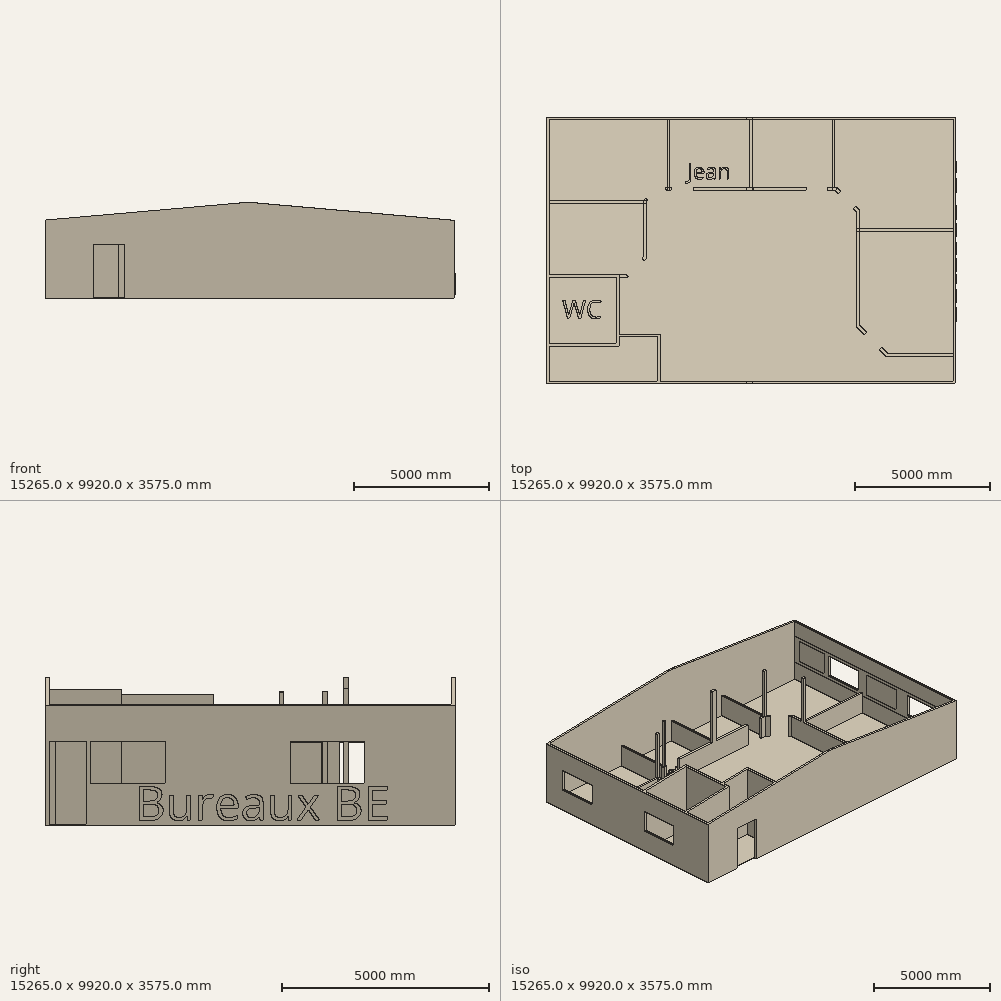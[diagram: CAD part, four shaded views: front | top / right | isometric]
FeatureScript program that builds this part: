
annotation { "Feature Type Name" : "Feature", "Feature Type Description" : "" }
export const myFeature = defineFeature(function(context is Context, id is Id, definition is map)
    precondition{}
    {
        {
            var Q0;
            Q0=qCreatedBy(makeId("Top.planeOp"),FACE);
            var sketch = newSketch(context, id + "F0", { "sketchPlane" : qUnion([Q0])});
            skLineSegment(sketch, "E0.bottom", {"start": v(0, 0) * mm, "end": v(-15040, 0) * mm});
            skLineSegment(sketch, "E0.top", {"start": v(0, 9720) * mm, "end": v(-15040, 9720) * mm});
            skLineSegment(sketch, "E0.left", {"start": v(0, 0) * mm, "end": v(0, 9720) * mm});
            skLineSegment(sketch, "E0.right", {"start": v(-15040, 0) * mm, "end": v(-15040, 9720) * mm});
            skSolve(sketch);
        }
        {
            var Q0;
            Q0 = qSketchRegion(id + "F0", true);
            extrude(context, id + "F1", {"entities" : qUnion([Q0]), "depth" : 25 * mm});
        }
        {
            var Q0;
            Q0=makeQuery(id+"F1.opExtrude","CAP_FACE",FACE,{"disambiguationData":[OSD([sQuery(id+"F0.wireOp",EDGE,"E0.bottom"),sQuery(id+"F0.wireOp",EDGE,"E0.top"),sQuery(id+"F0.wireOp",EDGE,"E0.left"),sQuery(id+"F0.wireOp",EDGE,"E0.right")])],"isStart":false});
            var sketch = newSketch(context, id + "F2", { "sketchPlane" : qUnion([Q0])});
            skLineSegment(sketch, "E1", {"start": v(-15040, 1300) * mm, "end": v(-12440, 1300) * mm});
            skLineSegment(sketch, "E2", {"start": v(-12440, 1300) * mm, "end": v(-12440, 1650) * mm});
            skLineSegment(sketch, "E3", {"start": v(-12440, 1650) * mm, "end": v(-10990, 1650) * mm});
            skLineSegment(sketch, "E4", {"start": v(-10990, 1650) * mm, "end": v(-10990, 0) * mm});
            skLineSegment(sketch, "E5", {"start": v(-10990, 0) * mm, "end": v(-10890, 0) * mm});
            skLineSegment(sketch, "E6", {"start": v(-10890, 0) * mm, "end": v(-10890, 1750) * mm});
            skLineSegment(sketch, "E7", {"start": v(-10890, 1750) * mm, "end": v(-12540, 1750) * mm});
            skLineSegment(sketch, "E8", {"start": v(-12540, 1750) * mm, "end": v(-12540, 1400) * mm});
            skLineSegment(sketch, "E9", {"start": v(-12540, 1400) * mm, "end": v(-15040, 1400) * mm});
            skLineSegment(sketch, "E10", {"start": v(-15040, 1400) * mm, "end": v(-15040, 1300) * mm});
            skLineSegment(sketch, "E11.bottom", {"start": v(-15040, 0) * mm, "end": v(0, 0) * mm});
            skLineSegment(sketch, "E11.top", {"start": v(-15040, 9720) * mm, "end": v(0, 9720) * mm});
            skLineSegment(sketch, "E11.left", {"start": v(-15040, 0) * mm, "end": v(-15040, 9720) * mm});
            skLineSegment(sketch, "E11.right", {"start": v(0, 0) * mm, "end": v(0, 9720) * mm});
            skLineSegment(sketch, "E12.bottom", {"start": v(100, 9820) * mm, "end": v(-15140, 9820) * mm});
            skLineSegment(sketch, "E12.top", {"start": v(100, -100) * mm, "end": v(-15140, -100) * mm});
            skLineSegment(sketch, "E12.left", {"start": v(100, 9820) * mm, "end": v(100, -100) * mm});
            skLineSegment(sketch, "E12.right", {"start": v(-15140, 9820) * mm, "end": v(-15140, -100) * mm});
            skLineSegment(sketch, "E13", {"start": v(0, 900) * mm, "end": v(-2479.9, 900) * mm});
            skLineSegment(sketch, "E14", {"start": v(-2479.9, 900) * mm, "end": v(-3615, 2035.1) * mm});
            skLineSegment(sketch, "E15", {"start": v(-3615, 2035.1) * mm, "end": v(-3615, 4846.83) * mm});
            skLineSegment(sketch, "E16.0", {"start": v(-3500, 2082.73) * mm, "end": v(-3500, 5555) * mm});
            skLineSegment(sketch, "E16.1", {"start": v(-2432.27, 1015) * mm, "end": v(-3500, 2082.73) * mm});
            skLineSegment(sketch, "E16.2", {"start": v(0, 1015) * mm, "end": v(-2432.27, 1015) * mm});
            skLineSegment(sketch, "E17", {"start": v(-3500, 5555) * mm, "end": v(0, 5555) * mm});
            skLineSegment(sketch, "E18", {"start": v(0, 5555) * mm, "end": v(0, 5670) * mm});
            skLineSegment(sketch, "E19", {"start": v(0, 5670) * mm, "end": v(-3500, 5670) * mm});
            skLineSegment(sketch, "E20", {"start": v(-3500, 5670) * mm, "end": v(-3500, 6371.47) * mm});
            skLineSegment(sketch, "E21", {"start": v(-3615, 4846.83) * mm, "end": v(-3615, 6323.84) * mm});
            skLineSegment(sketch, "E22", {"start": v(-3615, 6323.84) * mm, "end": v(-4396.16, 7105) * mm});
            skLineSegment(sketch, "E23", {"start": v(-4400, 7220) * mm, "end": v(-4400, 9720) * mm});
            skLineSegment(sketch, "E24", {"start": v(-4400, 9720) * mm, "end": v(-4475, 9720) * mm});
            skLineSegment(sketch, "E25", {"start": v(-4475, 9720) * mm, "end": v(-4475, 7220) * mm});
            skLineSegment(sketch, "E26", {"start": v(-4475, 7220) * mm, "end": v(-7475, 7220) * mm});
            skLineSegment(sketch, "E27", {"start": v(-4396.16, 7105) * mm, "end": v(-10610.2, 7105) * mm});
            skLineSegment(sketch, "E28", {"start": v(-4400, 7220) * mm, "end": v(-4348.53, 7220) * mm});
            skLineSegment(sketch, "E29", {"start": v(-4348.53, 7220) * mm, "end": v(-3500, 6371.47) * mm});
            skLineSegment(sketch, "E30", {"start": v(-7475, 7220) * mm, "end": v(-7475, 9720) * mm});
            skLineSegment(sketch, "E31", {"start": v(-7475, 9720) * mm, "end": v(-7565, 9720) * mm});
            skLineSegment(sketch, "E32", {"start": v(-7565, 9720) * mm, "end": v(-7565, 7220) * mm});
            skLineSegment(sketch, "E33", {"start": v(-7565, 7220) * mm, "end": v(-10565, 7220) * mm});
            skLineSegment(sketch, "E34", {"start": v(-10565, 7220) * mm, "end": v(-10565, 9720) * mm});
            skLineSegment(sketch, "E35", {"start": v(-10565, 9720) * mm, "end": v(-10640, 9720) * mm});
            skLineSegment(sketch, "E36", {"start": v(-10640, 9720) * mm, "end": v(-10640, 7220) * mm});
            skLineSegment(sketch, "E37", {"start": v(-10640, 7220) * mm, "end": v(-11540, 6720) * mm});
            skLineSegment(sketch, "E38", {"start": v(-11540, 6720) * mm, "end": v(-11540, 6720) * mm});
            skLineSegment(sketch, "E39", {"start": v(-11540, 6720) * mm, "end": v(-15040, 6720) * mm});
            skLineSegment(sketch, "E40", {"start": v(-15040, 6720) * mm, "end": v(-15040, 6605) * mm});
            skLineSegment(sketch, "E41", {"start": v(-15040, 6605) * mm, "end": v(-11540, 6605) * mm});
            skLineSegment(sketch, "E42", {"start": v(-11540, 6605) * mm, "end": v(-11540, 4595.6) * mm});
            skLineSegment(sketch, "E43", {"start": v(-11540, 4595.6) * mm, "end": v(-12165.6, 3970) * mm});
            skLineSegment(sketch, "E44", {"start": v(-12165.6, 3970) * mm, "end": v(-15040, 3970) * mm});
            skLineSegment(sketch, "E45", {"start": v(-15040, 3970) * mm, "end": v(-15040, 3855) * mm});
            skLineSegment(sketch, "E46", {"start": v(-15040, 3855) * mm, "end": v(-12117.96, 3855) * mm});
            skLineSegment(sketch, "E47", {"start": v(-12117.96, 3855) * mm, "end": v(-11425, 4547.96) * mm});
            skLineSegment(sketch, "E48", {"start": v(-11425, 4547.96) * mm, "end": v(-11425, 6652.33) * mm});
            skLineSegment(sketch, "E49", {"start": v(-11425, 6652.33) * mm, "end": v(-10610.2, 7105) * mm});
            skLineSegment(sketch, "E50", {"start": v(-12540, 1750) * mm, "end": v(-12540, 3855) * mm});
            skLineSegment(sketch, "E51", {"start": v(-12440, 1750) * mm, "end": v(-12440, 3855) * mm});
            skLineSegment(sketch, "E52", {"start": v(-12440, 3855) * mm, "end": v(-12540, 3855) * mm});
            skLineSegment(sketch, "E53", {"start": v(-12440, 1750) * mm, "end": v(-12540, 1750) * mm});
            skSolve(sketch);
        }
        {
            var Q0;
            Q0 = qSketchRegion(id + "F2", true);
            var Q1;
            {var subQ3=sQuery(id+"F2.wireOp",EDGE,"E1");Q1=makeQuery(id+"F2.imprint","IMPRINT",FACE,{"disambiguationData":[TD([[makeQuery(id+"F2.imprint","IMPRINT",EDGE,{"derivedFrom":subQ3}),1.0]])]});}
            var Q2;
            Q2=makeQuery(id+"F2.imprint","IMPRINT",FACE,{"disambiguationData":[TD([[makeQuery(id+"F2.imprint","IMPRINT",EDGE,{"derivedFrom":sQuery(id+"F2.wireOp",EDGE,"E50")}),-1.0]])]});
            var Q3;
            {var subQ2=sQuery(id+"F2.wireOp",EDGE,"E13");Q3=makeQuery(id+"F2.imprint","IMPRINT",FACE,{"disambiguationData":[TD([[makeQuery(id+"F2.imprint","IMPRINT",EDGE,{"derivedFrom":subQ2}),-1.0]])]});}
            extrude(context, id + "F3", {"entities" : qUnion([Q0, Q1, Q2, Q3]), "operationType" : NewBodyOperationType.ADD, "depth" : 3550 * mm, "hasSecondDirection" : true, "secondDirectionOppositeDirection" : true, "secondDirectionDepth" : 25 * mm});
        }
        {
            var Q0;
            Q0=makeQuery(id+"F3.opExtrude","SWEPT_FACE",FACE,{"disambiguationData":[OSD([sQuery(id+"F2.wireOp",EDGE,"E12.left")])]});
            var sketch = newSketch(context, id + "F4", { "sketchPlane" : qUnion([Q0])});
            skLineSegment(sketch, "E54.bottom", {"start": v(1000, 2025) * mm, "end": v(2800, 2025) * mm});
            skLineSegment(sketch, "E54.top", {"start": v(1000, 1025) * mm, "end": v(2800, 1025) * mm});
            skLineSegment(sketch, "E54.left", {"start": v(1000, 2025) * mm, "end": v(1000, 1025) * mm});
            skLineSegment(sketch, "E54.right", {"start": v(2800, 2025) * mm, "end": v(2800, 1025) * mm});
            skLineSegment(sketch, "E55.bottom", {"start": v(5830, 2025) * mm, "end": v(7630, 2025) * mm});
            skLineSegment(sketch, "E55.top", {"start": v(5830, 1025) * mm, "end": v(7630, 1025) * mm});
            skLineSegment(sketch, "E55.left", {"start": v(5830, 2025) * mm, "end": v(5830, 1025) * mm});
            skLineSegment(sketch, "E55.right", {"start": v(7630, 2025) * mm, "end": v(7630, 1025) * mm});
            skSolve(sketch);
        }
        {
            var Q0;
            Q0 = qSketchRegion(id + "F4", true);
            var Q1;
            {var subQ0=sQuery(id+"F2.wireOp",EDGE,"E11.right");Q1=makeQuery(id+"F3.opExtrude","SWEPT_FACE",FACE,{"disambiguationData":[OSD([subQ0]),TDD([makeQuery(id+"F2.imprint","IMPRINT",EDGE,{"disambiguationData":[TD([[makeQuery(id+"F2.imprint","INTERSECT",VERTEX,{"derivedFrom":[subQ0,sQuery(id+"F2.wireOp",EDGE,"E16.2")]}),-1.0]])],"derivedFrom":subQ0})])]});}
            extrude(context, id + "F5", {"entities" : qUnion([Q0]), "operationType" : NewBodyOperationType.REMOVE, "endBound" : BoundingType.UP_TO_SURFACE, "oppositeDirection" : true, "endBoundEntityFace" : qUnion([Q1]), "depth" : 25 * mm});
        }
        {
            var Q0;
            Q0=makeQuery(id+"F3.opExtrude","SWEPT_FACE",FACE,{"disambiguationData":[OSD([sQuery(id+"F2.wireOp",EDGE,"E12.right")])]});
            var sketch = newSketch(context, id + "F6", { "sketchPlane" : qUnion([Q0])});
            skLineSegment(sketch, "E56.bottom", {"start": v(-8820, 2000) * mm, "end": v(-7020, 2000) * mm});
            skLineSegment(sketch, "E56.top", {"start": v(-8820, 1000) * mm, "end": v(-7020, 1000) * mm});
            skLineSegment(sketch, "E56.left", {"start": v(-8820, 2000) * mm, "end": v(-8820, 1000) * mm});
            skLineSegment(sketch, "E56.right", {"start": v(-7020, 2000) * mm, "end": v(-7020, 1000) * mm});
            skLineSegment(sketch, "E57.bottom", {"start": v(-3810, 2000) * mm, "end": v(-2010, 2000) * mm});
            skLineSegment(sketch, "E57.top", {"start": v(-3810, 1000) * mm, "end": v(-2010, 1000) * mm});
            skLineSegment(sketch, "E57.left", {"start": v(-3810, 2000) * mm, "end": v(-3810, 1000) * mm});
            skLineSegment(sketch, "E57.right", {"start": v(-2010, 2000) * mm, "end": v(-2010, 1000) * mm});
            skSolve(sketch);
        }
        {
            var Q0;
            Q0 = qSketchRegion(id + "F6", true);
            var Q1;
            {var subQ0=sQuery(id+"F2.wireOp",EDGE,"E11.left");Q1=makeQuery(id+"F3.opExtrude","SWEPT_FACE",FACE,{"disambiguationData":[OSD([subQ0]),TDD([makeQuery(id+"F2.imprint","IMPRINT",EDGE,{"disambiguationData":[TD([[makeQuery(id+"F2.imprint","INTERSECT",VERTEX,{"derivedFrom":[subQ0,sQuery(id+"F2.wireOp",EDGE,"E40"),sQuery(id+"F2.wireOp",EDGE,"E41")]}),1.0]])],"derivedFrom":subQ0})])]});}
            extrude(context, id + "F7", {"entities" : qUnion([Q0]), "operationType" : NewBodyOperationType.REMOVE, "endBound" : BoundingType.UP_TO_SURFACE, "oppositeDirection" : true, "endBoundEntityFace" : qUnion([Q1]), "depth" : 25 * mm});
        }
        {
            var Q0;
            Q0=makeQuery(id+"F3.opExtrude","SWEPT_FACE",FACE,{"disambiguationData":[OSD([sQuery(id+"F2.wireOp",EDGE,"E12.top")])]});
            var sketch = newSketch(context, id + "F8", { "sketchPlane" : qUnion([Q0])});
            skLineSegment(sketch, "E58.bottom", {"start": v(-13340, 0) * mm, "end": v(-12190, 0) * mm});
            skLineSegment(sketch, "E58.top", {"start": v(-13340, 2000) * mm, "end": v(-12190, 2000) * mm});
            skLineSegment(sketch, "E58.left", {"start": v(-13340, 0) * mm, "end": v(-13340, 2000) * mm});
            skLineSegment(sketch, "E58.right", {"start": v(-12190, 0) * mm, "end": v(-12190, 2000) * mm});
            skSolve(sketch);
        }
        {
            var Q0;
            Q0 = qSketchRegion(id + "F8", true);
            var Q1;
            {var subQ0=sQuery(id+"F2.wireOp",EDGE,"E11.bottom");Q1=makeQuery(id+"F3.opExtrude","SWEPT_FACE",FACE,{"disambiguationData":[OSD([subQ0]),TDD([makeQuery(id+"F2.imprint","IMPRINT",EDGE,{"disambiguationData":[TD([[makeQuery(id+"F2.imprint","INTERSECT",VERTEX,{"derivedFrom":[subQ0,sQuery(id+"F2.wireOp",EDGE,"E11.left")]}),1.0]])],"derivedFrom":subQ0})])]});}
            extrude(context, id + "F9", {"entities" : qUnion([Q0]), "operationType" : NewBodyOperationType.REMOVE, "endBound" : BoundingType.UP_TO_SURFACE, "oppositeDirection" : true, "endBoundEntityFace" : qUnion([Q1]), "depth" : 25 * mm});
        }
        {
            var Q0;
            Q0=makeQuery(id+"F3.opExtrude","SWEPT_FACE",FACE,{"disambiguationData":[OSD([sQuery(id+"F2.wireOp",EDGE,"E6")])]});
            var sketch = newSketch(context, id + "F10", { "sketchPlane" : qUnion([Q0])});
            skLineSegment(sketch, "E59.bottom", {"start": v(930, 25) * mm, "end": v(130, 25) * mm});
            skLineSegment(sketch, "E59.top", {"start": v(930, 2025) * mm, "end": v(130, 2025) * mm});
            skLineSegment(sketch, "E59.left", {"start": v(930, 25) * mm, "end": v(930, 2025) * mm});
            skLineSegment(sketch, "E59.right", {"start": v(130, 25) * mm, "end": v(130, 2025) * mm});
            skSolve(sketch);
        }
        {
            var Q0;
            Q0 = qSketchRegion(id + "F10", true);
            extrude(context, id + "F11", {"entities" : qUnion([Q0]), "operationType" : NewBodyOperationType.REMOVE, "endBound" : BoundingType.UP_TO_NEXT, "oppositeDirection" : true, "depth" : 25 * mm});
        }
        {
            var Q0;
            Q0=makeQuery(id+"F3.opExtrude","SWEPT_FACE",FACE,{"disambiguationData":[OSD([sQuery(id+"F2.wireOp",EDGE,"E12.bottom")])]});
            var sketch = newSketch(context, id + "F12", { "sketchPlane" : qUnion([Q0])});
            skLineSegment(sketch, "E60", {"start": v(7680, 3575) * mm, "end": v(15140, 2919.97) * mm});
            skLineSegment(sketch, "E61", {"start": v(15140, 2919.97) * mm, "end": v(15140, 3575) * mm});
            skLineSegment(sketch, "E62", {"start": v(15140, 3575) * mm, "end": v(7680, 3575) * mm});
            skLineSegment(sketch, "E63", {"start": v(7480, 3575) * mm, "end": v(-100, 3575) * mm});
            skLineSegment(sketch, "E64", {"start": v(-100, 3575) * mm, "end": v(-100, 2909.44) * mm});
            skLineSegment(sketch, "E65", {"start": v(-100, 2909.44) * mm, "end": v(7480, 3575) * mm});
            skSolve(sketch);
        }
        {
            var Q0;
            Q0 = qSketchRegion(id + "F12", true);
            extrude(context, id + "F13", {"entities" : qUnion([Q0]), "operationType" : NewBodyOperationType.REMOVE, "endBound" : BoundingType.THROUGH_ALL, "oppositeDirection" : true, "depth" : 25 * mm});
        }
        {
            var Q0;
            {var subQ0=sQuery(id+"F2.wireOp",EDGE,"E11.right");Q0=makeQuery(id+"F3.opExtrude","SWEPT_FACE",FACE,{"disambiguationData":[OSD([subQ0]),TDD([makeQuery(id+"F2.imprint","IMPRINT",EDGE,{"disambiguationData":[TD([[makeQuery(id+"F2.imprint","INTERSECT",VERTEX,{"derivedFrom":[sQuery(id+"F2.wireOp",EDGE,"E11.bottom"),subQ0]}),-1.0]])],"derivedFrom":subQ0})])]});}
            var sketch = newSketch(context, id + "F14", { "sketchPlane" : qUnion([Q0])});
            skLineSegment(sketch, "E66.bottom", {"start": v(0, 25) * mm, "end": v(-900, 25) * mm});
            skLineSegment(sketch, "E66.top", {"start": v(0, 2025) * mm, "end": v(-900, 2025) * mm});
            skLineSegment(sketch, "E66.left", {"start": v(0, 25) * mm, "end": v(0, 2025) * mm});
            skLineSegment(sketch, "E66.right", {"start": v(-900, 25) * mm, "end": v(-900, 2025) * mm});
            skSolve(sketch);
        }
        {
            var Q0;
            Q0 = qSketchRegion(id + "F14", true);
            extrude(context, id + "F15", {"entities" : qUnion([Q0]), "operationType" : NewBodyOperationType.REMOVE, "endBound" : BoundingType.UP_TO_NEXT, "oppositeDirection" : true, "depth" : 25 * mm});
        }
        {
            var Q0;
            {var subQ0=sQuery(id+"F2.wireOp",EDGE,"E32");var subQ1=sQuery(id+"F2.wireOp",EDGE,"E27");var subQ2=sQuery(id+"F2.wireOp",EDGE,"E12.bottom");var subQ3=sQuery(id+"F2.wireOp",EDGE,"E11.top");var subQ4=sQuery(id+"F2.wireOp",EDGE,"E34");var subQ5=sQuery(id+"F2.wireOp",EDGE,"E33");Q0=makeQuery(id+"F13.boolean.opBoolean","SPLIT",FACE,{"disambiguationData":[TD([makeQuery(id+"F3.opExtrude","SWEPT_FACE",FACE,{"disambiguationData":[OSD([subQ2])]})])],"derivedFrom":makeQuery(id+"F3.opExtrude","CAP_FACE",FACE,{"disambiguationData":[OSD([sQuery(id+"F2.wireOp",EDGE,"E1"),sQuery(id+"F2.wireOp",EDGE,"E2"),sQuery(id+"F2.wireOp",EDGE,"E3"),sQuery(id+"F2.wireOp",EDGE,"E4"),sQuery(id+"F2.wireOp",EDGE,"E6"),sQuery(id+"F2.wireOp",EDGE,"E7"),sQuery(id+"F2.wireOp",EDGE,"E8"),sQuery(id+"F2.wireOp",EDGE,"E9"),sQuery(id+"F2.wireOp",EDGE,"E11.bottom"),subQ3,sQuery(id+"F2.wireOp",EDGE,"E11.left"),sQuery(id+"F2.wireOp",EDGE,"E11.right"),subQ2,sQuery(id+"F2.wireOp",EDGE,"E12.top"),sQuery(id+"F2.wireOp",EDGE,"E12.left"),sQuery(id+"F2.wireOp",EDGE,"E12.right"),sQuery(id+"F2.wireOp",EDGE,"E13"),sQuery(id+"F2.wireOp",EDGE,"E14"),sQuery(id+"F2.wireOp",EDGE,"E15"),sQuery(id+"F2.wireOp",EDGE,"E16.0"),sQuery(id+"F2.wireOp",EDGE,"E16.1"),sQuery(id+"F2.wireOp",EDGE,"E16.2"),sQuery(id+"F2.wireOp",EDGE,"E17"),sQuery(id+"F2.wireOp",EDGE,"E19"),sQuery(id+"F2.wireOp",EDGE,"E20"),sQuery(id+"F2.wireOp",EDGE,"E21"),sQuery(id+"F2.wireOp",EDGE,"E22"),sQuery(id+"F2.wireOp",EDGE,"E23"),sQuery(id+"F2.wireOp",EDGE,"E25"),sQuery(id+"F2.wireOp",EDGE,"E26"),subQ1,sQuery(id+"F2.wireOp",EDGE,"E28"),sQuery(id+"F2.wireOp",EDGE,"E29"),sQuery(id+"F2.wireOp",EDGE,"E30"),subQ0,subQ5,subQ4,sQuery(id+"F2.wireOp",EDGE,"E36"),sQuery(id+"F2.wireOp",EDGE,"E37"),sQuery(id+"F2.wireOp",EDGE,"E38"),sQuery(id+"F2.wireOp",EDGE,"E39"),sQuery(id+"F2.wireOp",EDGE,"E41"),sQuery(id+"F2.wireOp",EDGE,"E42"),sQuery(id+"F2.wireOp",EDGE,"E43"),sQuery(id+"F2.wireOp",EDGE,"E44"),sQuery(id+"F2.wireOp",EDGE,"E46"),sQuery(id+"F2.wireOp",EDGE,"E47"),sQuery(id+"F2.wireOp",EDGE,"E48"),sQuery(id+"F2.wireOp",EDGE,"E49"),sQuery(id+"F2.wireOp",EDGE,"E50"),sQuery(id+"F2.wireOp",EDGE,"E51")])],"isStart":false})});}
            var sketch = newSketch(context, id + "F16", { "sketchPlane" : qUnion([Q0])});
            skLineSegment(sketch, "E67.bottom", {"start": v(-15040, 9720) * mm, "end": v(0, 9720) * mm});
            skLineSegment(sketch, "E67.top", {"start": v(-15040, 0) * mm, "end": v(0, 0) * mm});
            skLineSegment(sketch, "E67.left", {"start": v(-15040, 9720) * mm, "end": v(-15040, 0) * mm});
            skLineSegment(sketch, "E67.right", {"start": v(0, 9720) * mm, "end": v(0, 0) * mm});
            skLineSegment(sketch, "E68", {"start": v(-15040, 3970) * mm, "end": v(-12440, 3970) * mm});
            skLineSegment(sketch, "E69", {"start": v(-12440, 3855) * mm, "end": v(-12440, 3970) * mm});
            skLineSegment(sketch, "E70", {"start": v(-12440, 3855) * mm, "end": v(-6280.37, 0) * mm});
            skLineSegment(sketch, "E71", {"start": v(-7426.32, 9720) * mm, "end": v(-7814.56, 9720) * mm});
            skLineSegment(sketch, "E72.bottom", {"start": v(-11540, 6720) * mm, "end": v(-11425, 6720) * mm});
            skLineSegment(sketch, "E72.top", {"start": v(-11540, 6605) * mm, "end": v(-11425, 6605) * mm});
            skLineSegment(sketch, "E72.left", {"start": v(-11540, 6720) * mm, "end": v(-11540, 6605) * mm});
            skLineSegment(sketch, "E72.right", {"start": v(-11425, 6720) * mm, "end": v(-11425, 6605) * mm});
            skLineSegment(sketch, "E73.bottom", {"start": v(-10640, 7220) * mm, "end": v(-10565, 7220) * mm});
            skLineSegment(sketch, "E73.top", {"start": v(-10640, 7105) * mm, "end": v(-10565, 7105) * mm});
            skLineSegment(sketch, "E73.left", {"start": v(-10640, 7220) * mm, "end": v(-10640, 7105) * mm});
            skLineSegment(sketch, "E73.right", {"start": v(-10565, 7220) * mm, "end": v(-10565, 7105) * mm});
            skLineSegment(sketch, "E74.bottom", {"start": v(-4348.53, 7220) * mm, "end": v(-4475, 7220) * mm});
            skLineSegment(sketch, "E74.top", {"start": v(-4348.53, 7105) * mm, "end": v(-4475, 7105) * mm});
            skLineSegment(sketch, "E74.left", {"start": v(-4348.53, 7220) * mm, "end": v(-4348.53, 7105) * mm});
            skLineSegment(sketch, "E74.right", {"start": v(-4475, 7220) * mm, "end": v(-4475, 7105) * mm});
            skLineSegment(sketch, "E75.bottom", {"start": v(-3615, 5670) * mm, "end": v(-3500, 5670) * mm});
            skLineSegment(sketch, "E75.top", {"start": v(-3615, 5555) * mm, "end": v(-3500, 5555) * mm});
            skLineSegment(sketch, "E75.left", {"start": v(-3615, 5670) * mm, "end": v(-3615, 5555) * mm});
            skLineSegment(sketch, "E75.right", {"start": v(-3500, 5670) * mm, "end": v(-3500, 5555) * mm});
            skLineSegment(sketch, "E76.bottom", {"start": v(-7565, 7220) * mm, "end": v(-7450, 7220) * mm});
            skLineSegment(sketch, "E76.top", {"start": v(-7565, 7105) * mm, "end": v(-7450, 7105) * mm});
            skLineSegment(sketch, "E76.left", {"start": v(-7565, 7220) * mm, "end": v(-7565, 7105) * mm});
            skLineSegment(sketch, "E76.right", {"start": v(-7450, 7220) * mm, "end": v(-7450, 7105) * mm});
            skSolve(sketch);
        }
        {
            var Q0;
            {var subQ21=sQuery(id+"F16.wireOp",EDGE,"E67.right");Q0=makeQuery(id+"F16.imprint","IMPRINT",FACE,{"disambiguationData":[TD([[makeQuery(id+"F16.imprint","IMPRINT",EDGE,{"derivedFrom":subQ21}),-1.0]])]});}
            var Q1;
            {var subQ3=sQuery(id+"F2.wireOp",EDGE,"E32");var subQ4=makeQuery(id+"F3.opExtrude","CAP_EDGE",EDGE,{"disambiguationData":[OSD([subQ3])],"isStart":false});Q1=makeQuery(id+"F16.imprint","IMPRINT",FACE,{"disambiguationData":[TD([[makeQuery(id+"F16.imprint","IMPRINT",EDGE,{"derivedFrom":subQ4}),1.0]])]});}
            extrude(context, id + "F17", {"entities" : qUnion([Q0, Q1]), "operationType" : NewBodyOperationType.REMOVE, "oppositeDirection" : true, "depth" : 2550 * mm});
        }
        {
            var Q0;
            {var subQ0=sQuery(id+"F2.wireOp",EDGE,"E11.top");var subQ2=sQuery(id+"F2.wireOp",EDGE,"E31");var subQ3=sQuery(id+"F2.wireOp",EDGE,"E24");Q0=makeQuery(id+"F17.boolean.opBoolean","MERGE",FACE,{"derivedFrom":[makeQuery(id+"F3.opExtrude","SWEPT_FACE",FACE,{"disambiguationData":[OSD([subQ0]),TDD([makeQuery(id+"F2.imprint","IMPRINT",EDGE,{"disambiguationData":[TD([[makeQuery(id+"F2.imprint","INTERSECT",VERTEX,{"derivedFrom":[subQ0,sQuery(id+"F2.wireOp",EDGE,"E11.right")]}),-1.0]])],"derivedFrom":subQ0})])]}),makeQuery(id+"F3.opExtrude","SWEPT_FACE",FACE,{"disambiguationData":[OSD([subQ0]),TDD([makeQuery(id+"F2.imprint","IMPRINT",EDGE,{"disambiguationData":[TD([[makeQuery(id+"F2.imprint","INTERSECT",VERTEX,{"derivedFrom":[subQ0,subQ3,sQuery(id+"F2.wireOp",EDGE,"E25")]}),-1.0]])],"derivedFrom":subQ0})])]}),makeQuery(id+"F3.opExtrude","SWEPT_FACE",FACE,{"disambiguationData":[OSD([subQ0]),TDD([makeQuery(id+"F2.imprint","IMPRINT",EDGE,{"disambiguationData":[TD([[makeQuery(id+"F2.imprint","INTERSECT",VERTEX,{"derivedFrom":[subQ0,subQ2,sQuery(id+"F2.wireOp",EDGE,"E32")]}),-1.0]])],"derivedFrom":subQ0})])]}),makeQuery(id+"F3.opExtrude","SWEPT_FACE",FACE,{"disambiguationData":[OSD([subQ0]),TDD([makeQuery(id+"F2.imprint","IMPRINT",EDGE,{"disambiguationData":[TD([[makeQuery(id+"F2.imprint","INTERSECT",VERTEX,{"derivedFrom":[subQ0,sQuery(id+"F2.wireOp",EDGE,"E11.left")]}),1.0]])],"derivedFrom":subQ0})])]}),makeQuery(id+"F17.opExtrude","SWEPT_FACE",FACE,{"disambiguationData":[OSD([sQuery(id+"F16.wireOp",EDGE,"E67.bottom"),sQuery(id+"F16.wireOp",EDGE,"E71")])]})]});}
            var sketch = newSketch(context, id + "F18", { "sketchPlane" : qUnion([Q0])});
            skLineSegment(sketch, "E77", {"start": v(-15040, 25) * mm, "end": v(0, 0) * mm});
            skLineSegment(sketch, "E78", {"start": v(0, 0) * mm, "end": v(0, 2918.22) * mm});
            skLineSegment(sketch, "E79", {"start": v(0, 2918.22) * mm, "end": v(-7480, 3575) * mm});
            skLineSegment(sketch, "E80", {"start": v(-7480, 3575) * mm, "end": v(-7680, 3575) * mm});
            skLineSegment(sketch, "E81", {"start": v(-7680, 3575) * mm, "end": v(-15040, 2928.75) * mm});
            skLineSegment(sketch, "E82", {"start": v(-15040, 2928.75) * mm, "end": v(-15040, 25) * mm});
            skSolve(sketch);
        }
        {
            var Q0;
            Q0 = qSketchRegion(id + "F18", true);
            extrude(context, id + "F19", {"entities" : qUnion([Q0]), "depth" : 1 * mm});
        }
        {
            var Q0;
            {var subQ0=sQuery(id+"F2.wireOp",EDGE,"E11.bottom");Q0=makeQuery(id+"F15.boolean.opBoolean","MERGE",FACE,{"derivedFrom":[makeQuery(id+"F3.opExtrude","SWEPT_FACE",FACE,{"disambiguationData":[OSD([subQ0]),TDD([makeQuery(id+"F2.imprint","IMPRINT",EDGE,{"disambiguationData":[TD([[makeQuery(id+"F2.imprint","INTERSECT",VERTEX,{"derivedFrom":[subQ0,sQuery(id+"F2.wireOp",EDGE,"E11.right")]}),-1.0]])],"derivedFrom":subQ0})])]})],"fromTools":[makeQuery(id+"F15.opExtrude","SWEPT_FACE",FACE,{"disambiguationData":[OSD([sQuery(id+"F14.wireOp",EDGE,"E66.left")])]})]});}
            var sketch = newSketch(context, id + "F20", { "sketchPlane" : qUnion([Q0])});
            skLineSegment(sketch, "E83", {"start": v(0, 2918.22) * mm, "end": v(7480, 3575) * mm});
            skLineSegment(sketch, "E84", {"start": v(7480, 3575) * mm, "end": v(7680, 3575) * mm});
            skLineSegment(sketch, "E85", {"start": v(7680, 3575) * mm, "end": v(15040, 2928.75) * mm});
            skLineSegment(sketch, "E86", {"start": v(15040, 2928.75) * mm, "end": v(15040, 0) * mm});
            skLineSegment(sketch, "E87", {"start": v(15040, 0) * mm, "end": v(-100, 25) * mm});
            skLineSegment(sketch, "E88", {"start": v(-100, 25) * mm, "end": v(-100, 2918.22) * mm});
            skLineSegment(sketch, "E89", {"start": v(-100, 2918.22) * mm, "end": v(0, 2918.22) * mm});
            skLineSegment(sketch, "E90.bottom", {"start": v(12190, 4.7) * mm, "end": v(13340, 4.7) * mm});
            skLineSegment(sketch, "E90.top", {"start": v(12190, 2000) * mm, "end": v(13340, 2000) * mm});
            skLineSegment(sketch, "E90.left", {"start": v(12190, 4.7) * mm, "end": v(12190, 2000) * mm});
            skLineSegment(sketch, "E90.right", {"start": v(13340, 4.7) * mm, "end": v(13340, 2000) * mm});
            skSolve(sketch);
        }
        {
            var Q0;
            Q0 = qSketchRegion(id + "F20", true);
            extrude(context, id + "F21", {"entities" : qUnion([Q0]), "depth" : 1 * mm});
        }
        {
            var Q0;
            {var subQ0=sQuery(id+"F2.wireOp",EDGE,"E11.right");Q0=makeQuery(id+"F17.boolean.opBoolean","MERGE",FACE,{"derivedFrom":[makeQuery(id+"F3.opExtrude","SWEPT_FACE",FACE,{"disambiguationData":[OSD([subQ0]),TDD([makeQuery(id+"F2.imprint","IMPRINT",EDGE,{"disambiguationData":[TD([[makeQuery(id+"F2.imprint","INTERSECT",VERTEX,{"derivedFrom":[subQ0,sQuery(id+"F2.wireOp",EDGE,"E16.2")]}),-1.0]])],"derivedFrom":subQ0})])]}),makeQuery(id+"F3.opExtrude","SWEPT_FACE",FACE,{"disambiguationData":[OSD([subQ0]),TDD([makeQuery(id+"F2.imprint","IMPRINT",EDGE,{"disambiguationData":[TD([[makeQuery(id+"F2.imprint","INTERSECT",VERTEX,{"derivedFrom":[sQuery(id+"F2.wireOp",EDGE,"E11.top"),subQ0]}),1.0]])],"derivedFrom":subQ0})])]}),makeQuery(id+"F3.opExtrude","SWEPT_FACE",FACE,{"disambiguationData":[OSD([subQ0]),TDD([makeQuery(id+"F2.imprint","IMPRINT",EDGE,{"disambiguationData":[TD([[makeQuery(id+"F2.imprint","INTERSECT",VERTEX,{"derivedFrom":[sQuery(id+"F2.wireOp",EDGE,"E11.bottom"),subQ0]}),-1.0]])],"derivedFrom":subQ0})])]}),makeQuery(id+"F17.opExtrude","SWEPT_FACE",FACE,{"disambiguationData":[OSD([sQuery(id+"F16.wireOp",EDGE,"E67.right")])]})]});}
            var sketch = newSketch(context, id + "F22", { "sketchPlane" : qUnion([Q0])});
            skLineSegment(sketch, "E91", {"start": v(-9720, 2918.22) * mm, "end": v(-9720, 25) * mm});
            skLineSegment(sketch, "E92", {"start": v(-9720, 25) * mm, "end": v(0, 25) * mm});
            skLineSegment(sketch, "E93", {"start": v(0, 25) * mm, "end": v(0, 2918.22) * mm});
            skLineSegment(sketch, "E94", {"start": v(0, 2918.22) * mm, "end": v(-9720, 2918.22) * mm});
            skLineSegment(sketch, "E95.bottom", {"start": v(-7630, 2025) * mm, "end": v(-5830, 2025) * mm});
            skLineSegment(sketch, "E95.top", {"start": v(-7630, 1025) * mm, "end": v(-5830, 1025) * mm});
            skLineSegment(sketch, "E95.left", {"start": v(-7630, 2025) * mm, "end": v(-7630, 1025) * mm});
            skLineSegment(sketch, "E95.right", {"start": v(-5830, 2025) * mm, "end": v(-5830, 1025) * mm});
            skLineSegment(sketch, "E96.bottom", {"start": v(-2800, 2025) * mm, "end": v(-1000, 2025) * mm});
            skLineSegment(sketch, "E96.top", {"start": v(-2800, 1025) * mm, "end": v(-1000, 1025) * mm});
            skLineSegment(sketch, "E96.left", {"start": v(-2800, 2025) * mm, "end": v(-2800, 1025) * mm});
            skLineSegment(sketch, "E96.right", {"start": v(-1000, 2025) * mm, "end": v(-1000, 1025) * mm});
            skLineSegment(sketch, "E97.bottom", {"start": v(-900, 2025) * mm, "end": v(0, 2025) * mm});
            skLineSegment(sketch, "E97.top", {"start": v(-900, 25) * mm, "end": v(0, 25) * mm});
            skLineSegment(sketch, "E97.left", {"start": v(-900, 2025) * mm, "end": v(-900, 25) * mm});
            skLineSegment(sketch, "E97.right", {"start": v(0, 2025) * mm, "end": v(0, 25) * mm});
            skLineSegment(sketch, "E98.bottom", {"start": v(-7870.81, 2025) * mm, "end": v(-9428.7, 2025) * mm});
            skLineSegment(sketch, "E98.top", {"start": v(-7870.81, 1025) * mm, "end": v(-9428.7, 1025) * mm});
            skLineSegment(sketch, "E98.left", {"start": v(-7870.81, 2025) * mm, "end": v(-7870.81, 1025) * mm});
            skLineSegment(sketch, "E98.right", {"start": v(-9428.7, 2025) * mm, "end": v(-9428.7, 1025) * mm});
            skLineSegment(sketch, "E99.bottom", {"start": v(-5316.56, 2025) * mm, "end": v(-3456.7, 2025) * mm});
            skLineSegment(sketch, "E99.top", {"start": v(-5316.56, 1025) * mm, "end": v(-3456.7, 1025) * mm});
            skLineSegment(sketch, "E99.left", {"start": v(-5316.56, 2025) * mm, "end": v(-5316.56, 1025) * mm});
            skLineSegment(sketch, "E99.right", {"start": v(-3456.7, 2025) * mm, "end": v(-3456.7, 1025) * mm});
            skSolve(sketch);
        }
        {
            var Q0;
            {var subQ13=sQuery(id+"F22.wireOp",EDGE,"E91");Q0=makeQuery(id+"F22.imprint","IMPRINT",FACE,{"disambiguationData":[TD([[makeQuery(id+"F22.imprint","IMPRINT",EDGE,{"derivedFrom":subQ13}),1.0]])]});}
            extrude(context, id + "F23", {"entities" : qUnion([Q0]), "depth" : 1 * mm});
        }
        {
            var Q0;
            Q0=makeQuery(id+"F23.opExtrude","CAP_FACE",FACE,{"disambiguationData":[OSD([sQuery(id+"F22.wireOp",EDGE,"E91"),sQuery(id+"F22.wireOp",EDGE,"E92"),sQuery(id+"F22.wireOp",EDGE,"E93"),sQuery(id+"F22.wireOp",EDGE,"E94"),sQuery(id+"F22.wireOp",EDGE,"E95.bottom"),sQuery(id+"F22.wireOp",EDGE,"E95.top"),sQuery(id+"F22.wireOp",EDGE,"E95.left"),sQuery(id+"F22.wireOp",EDGE,"E95.right"),sQuery(id+"F22.wireOp",EDGE,"E96.bottom"),sQuery(id+"F22.wireOp",EDGE,"E96.top"),sQuery(id+"F22.wireOp",EDGE,"E96.left"),sQuery(id+"F22.wireOp",EDGE,"E96.right"),sQuery(id+"F22.wireOp",EDGE,"E97.top"),sQuery(id+"F22.wireOp",EDGE,"E97.right"),sQuery(id+"F22.wireOp",EDGE,"E98.bottom"),sQuery(id+"F22.wireOp",EDGE,"E98.top"),sQuery(id+"F22.wireOp",EDGE,"E98.left"),sQuery(id+"F22.wireOp",EDGE,"E98.right"),sQuery(id+"F22.wireOp",EDGE,"E99.bottom"),sQuery(id+"F22.wireOp",EDGE,"E99.top"),sQuery(id+"F22.wireOp",EDGE,"E99.left"),sQuery(id+"F22.wireOp",EDGE,"E99.right")])],"isStart":false});
            var sketch = newSketch(context, id + "F24", { "sketchPlane" : qUnion([Q0])});
            skLineSegment(sketch, "E100", {"start": v(-9720, 2175) * mm, "end": v(0, 2175) * mm});
            skLineSegment(sketch, "E101", {"start": v(0, 2175) * mm, "end": v(0, 875) * mm});
            skLineSegment(sketch, "E102", {"start": v(0, 875) * mm, "end": v(-9720, 875) * mm});
            skLineSegment(sketch, "E103", {"start": v(-9720, 875) * mm, "end": v(-9720, 2175) * mm});
            skSolve(sketch);
        }
        {
            var Q0;
            Q0=makeQuery(id+"F24.imprint","IMPRINT",FACE,{"disambiguationData":[TD([[makeQuery(id+"F24.imprint","IMPRINT",EDGE,{"derivedFrom":sQuery(id+"F24.wireOp",EDGE,"E100")}),-1.0]])]});
            extrude(context, id + "F25", {"entities" : qUnion([Q0]), "depth" : 1 * mm});
        }
        {
            var Q0;
            {var subQ0=sQuery(id+"F2.wireOp",EDGE,"E11.left");Q0=makeQuery(id+"F3.opExtrude","SWEPT_FACE",FACE,{"disambiguationData":[OSD([subQ0]),TDD([makeQuery(id+"F2.imprint","IMPRINT",EDGE,{"disambiguationData":[TD([[makeQuery(id+"F2.imprint","INTERSECT",VERTEX,{"derivedFrom":[sQuery(id+"F2.wireOp",EDGE,"E11.bottom"),subQ0]}),-1.0]])],"derivedFrom":subQ0})])]});}
            var sketch = newSketch(context, id + "F26", { "sketchPlane" : qUnion([Q0])});
            skLineSegment(sketch, "E104.bottom", {"start": v(1400, 2928.75) * mm, "end": v(9719, 2928.75) * mm});
            skLineSegment(sketch, "E104.top", {"start": v(1400, 0) * mm, "end": v(9719, 0) * mm});
            skLineSegment(sketch, "E104.left", {"start": v(1400, 2928.75) * mm, "end": v(1400, 0) * mm});
            skLineSegment(sketch, "E104.right", {"start": v(9719, 2928.75) * mm, "end": v(9719, 0) * mm});
            skLineSegment(sketch, "E105.bottom", {"start": v(2010, 2000) * mm, "end": v(3810, 2000) * mm});
            skLineSegment(sketch, "E105.top", {"start": v(2010, 1000) * mm, "end": v(3810, 1000) * mm});
            skLineSegment(sketch, "E105.left", {"start": v(2010, 2000) * mm, "end": v(2010, 1000) * mm});
            skLineSegment(sketch, "E105.right", {"start": v(3810, 2000) * mm, "end": v(3810, 1000) * mm});
            skLineSegment(sketch, "E106.bottom", {"start": v(7020, 2000) * mm, "end": v(8820, 2000) * mm});
            skLineSegment(sketch, "E106.top", {"start": v(7020, 1000) * mm, "end": v(8820, 1000) * mm});
            skLineSegment(sketch, "E106.left", {"start": v(7020, 2000) * mm, "end": v(7020, 1000) * mm});
            skLineSegment(sketch, "E106.right", {"start": v(8820, 2000) * mm, "end": v(8820, 1000) * mm});
            skLineSegment(sketch, "E107.bottom", {"start": v(4205.58, 2000) * mm, "end": v(6570.47, 2000) * mm});
            skLineSegment(sketch, "E107.top", {"start": v(4205.58, 1000) * mm, "end": v(6570.47, 1000) * mm});
            skLineSegment(sketch, "E107.left", {"start": v(4205.58, 2000) * mm, "end": v(4205.58, 1000) * mm});
            skLineSegment(sketch, "E107.right", {"start": v(6570.47, 2000) * mm, "end": v(6570.47, 1000) * mm});
            skLineSegment(sketch, "E108.bottom", {"start": v(8990.26, 2000) * mm, "end": v(9634.48, 2000) * mm});
            skLineSegment(sketch, "E108.top", {"start": v(8990.26, 1000) * mm, "end": v(9634.48, 1000) * mm});
            skLineSegment(sketch, "E108.left", {"start": v(8990.26, 2000) * mm, "end": v(8990.26, 1000) * mm});
            skLineSegment(sketch, "E108.right", {"start": v(9634.48, 2000) * mm, "end": v(9634.48, 1000) * mm});
            skSolve(sketch);
        }
        {
            var Q0;
            Q0=makeQuery(id+"F26.imprint","IMPRINT",FACE,{"disambiguationData":[TD([[makeQuery(id+"F26.imprint","IMPRINT",EDGE,{"derivedFrom":sQuery(id+"F26.wireOp",EDGE,"E104.bottom")}),-1.0]])]});
            extrude(context, id + "F27", {"entities" : qUnion([Q0]), "depth" : 1 * mm});
        }
        {
            var Q0;
            Q0=makeQuery(id+"F27.opExtrude","CAP_FACE",FACE,{"disambiguationData":[OSD([sQuery(id+"F26.wireOp",EDGE,"E104.bottom"),sQuery(id+"F26.wireOp",EDGE,"E104.top"),sQuery(id+"F26.wireOp",EDGE,"E104.left"),sQuery(id+"F26.wireOp",EDGE,"E104.right"),sQuery(id+"F26.wireOp",EDGE,"E105.bottom"),sQuery(id+"F26.wireOp",EDGE,"E105.top"),sQuery(id+"F26.wireOp",EDGE,"E105.left"),sQuery(id+"F26.wireOp",EDGE,"E105.right"),sQuery(id+"F26.wireOp",EDGE,"E106.bottom"),sQuery(id+"F26.wireOp",EDGE,"E106.top"),sQuery(id+"F26.wireOp",EDGE,"E106.left"),sQuery(id+"F26.wireOp",EDGE,"E106.right"),sQuery(id+"F26.wireOp",EDGE,"E107.bottom"),sQuery(id+"F26.wireOp",EDGE,"E107.top"),sQuery(id+"F26.wireOp",EDGE,"E107.left"),sQuery(id+"F26.wireOp",EDGE,"E107.right"),sQuery(id+"F26.wireOp",EDGE,"E108.bottom"),sQuery(id+"F26.wireOp",EDGE,"E108.top"),sQuery(id+"F26.wireOp",EDGE,"E108.left"),sQuery(id+"F26.wireOp",EDGE,"E108.right")])],"isStart":false});
            var sketch = newSketch(context, id + "F28", { "sketchPlane" : qUnion([Q0])});
            skLineSegment(sketch, "E109.bottom", {"start": v(9719, 2150) * mm, "end": v(1400, 2150) * mm});
            skLineSegment(sketch, "E109.top", {"start": v(9719, 850) * mm, "end": v(1400, 850) * mm});
            skLineSegment(sketch, "E109.left", {"start": v(9719, 2150) * mm, "end": v(9719, 850) * mm});
            skLineSegment(sketch, "E109.right", {"start": v(1400, 2150) * mm, "end": v(1400, 850) * mm});
            skSolve(sketch);
        }
        {
            var Q0;
            Q0=makeQuery(id+"F28.imprint","IMPRINT",FACE,{"disambiguationData":[TD([[makeQuery(id+"F28.imprint","IMPRINT",EDGE,{"derivedFrom":sQuery(id+"F28.wireOp",EDGE,"E109.bottom")}),1.0]])]});
            extrude(context, id + "F29", {"entities" : qUnion([Q0]), "depth" : 1 * mm});
        }
        {
            var Q0;
            Q0=makeQuery(id+"F21.opExtrude","CAP_FACE",FACE,{"disambiguationData":[OSD([sQuery(id+"F20.wireOp",EDGE,"E83"),sQuery(id+"F20.wireOp",EDGE,"E84"),sQuery(id+"F20.wireOp",EDGE,"E85"),sQuery(id+"F20.wireOp",EDGE,"E86"),sQuery(id+"F20.wireOp",EDGE,"E87"),sQuery(id+"F20.wireOp",EDGE,"E88"),sQuery(id+"F20.wireOp",EDGE,"E89")])],"isStart":true});
            var sketch = newSketch(context, id + "F30", { "sketchPlane" : qUnion([Q0])});
            skLineSegment(sketch, "E110.bottom", {"start": v(-13340, 0) * mm, "end": v(-12190, 0) * mm});
            skLineSegment(sketch, "E110.top", {"start": v(-13340, 2000) * mm, "end": v(-12190, 2000) * mm});
            skLineSegment(sketch, "E110.left", {"start": v(-13340, 0) * mm, "end": v(-13340, 2000) * mm});
            skLineSegment(sketch, "E110.right", {"start": v(-12190, 0) * mm, "end": v(-12190, 2000) * mm});
            skSolve(sketch);
        }
        {
            var Q0;
            Q0 = qSketchRegion(id + "F30", true);
            var Q1;
            Q1=makeQuery(id+"F21.opExtrude","CAP_FACE",FACE,{"disambiguationData":[OSD([sQuery(id+"F20.wireOp",EDGE,"E83"),sQuery(id+"F20.wireOp",EDGE,"E84"),sQuery(id+"F20.wireOp",EDGE,"E85"),sQuery(id+"F20.wireOp",EDGE,"E86"),sQuery(id+"F20.wireOp",EDGE,"E87"),sQuery(id+"F20.wireOp",EDGE,"E88"),sQuery(id+"F20.wireOp",EDGE,"E89")])],"isStart":false});
            extrude(context, id + "F31", {"entities" : qUnion([Q0]), "operationType" : NewBodyOperationType.REMOVE, "endBound" : BoundingType.UP_TO_SURFACE, "oppositeDirection" : true, "endBoundEntityFace" : qUnion([Q1]), "depth" : 25 * mm});
        }
        {
            var Q0;
            {var subQ0=sQuery(id+"F16.wireOp",EDGE,"E69");var subQ1=sQuery(id+"F16.wireOp",EDGE,"E72.right");var subQ2=sQuery(id+"F16.wireOp",EDGE,"E72.left");var subQ3=sQuery(id+"F16.wireOp",EDGE,"E72.top");var subQ4=makeQuery(id+"F17.opExtrude","CAP_FACE",FACE,{"disambiguationData":[OSD([sQuery(id+"F2.wireOp",EDGE,"E12.bottom"),sQuery(id+"F2.wireOp",EDGE,"E27"),sQuery(id+"F2.wireOp",EDGE,"E33"),sQuery(id+"F12.wireOp",EDGE,"E60"),sQuery(id+"F12.wireOp",EDGE,"E62"),sQuery(id+"F16.wireOp",EDGE,"E67.bottom"),sQuery(id+"F16.wireOp",EDGE,"E67.top"),sQuery(id+"F16.wireOp",EDGE,"E67.left"),sQuery(id+"F16.wireOp",EDGE,"E67.right"),sQuery(id+"F16.wireOp",EDGE,"E68"),subQ0,sQuery(id+"F16.wireOp",EDGE,"E70"),sQuery(id+"F16.wireOp",EDGE,"E71"),sQuery(id+"F16.wireOp",EDGE,"E72.bottom"),subQ3,subQ2,subQ1,sQuery(id+"F16.wireOp",EDGE,"E73.bottom"),sQuery(id+"F16.wireOp",EDGE,"E73.top"),sQuery(id+"F16.wireOp",EDGE,"E73.left"),sQuery(id+"F16.wireOp",EDGE,"E73.right"),sQuery(id+"F16.wireOp",EDGE,"E74.bottom"),sQuery(id+"F16.wireOp",EDGE,"E74.top"),sQuery(id+"F16.wireOp",EDGE,"E74.left"),sQuery(id+"F16.wireOp",EDGE,"E74.right"),sQuery(id+"F16.wireOp",EDGE,"E75.bottom"),sQuery(id+"F16.wireOp",EDGE,"E75.top"),sQuery(id+"F16.wireOp",EDGE,"E75.left"),sQuery(id+"F16.wireOp",EDGE,"E75.right"),sQuery(id+"F16.wireOp",EDGE,"E76.bottom"),sQuery(id+"F16.wireOp",EDGE,"E76.top"),sQuery(id+"F16.wireOp",EDGE,"E76.right")])],"isStart":false});var subQ5=sQuery(id+"F2.wireOp",EDGE,"E51");var subQ6=sQuery(id+"F2.wireOp",EDGE,"E47");var subQ7=sQuery(id+"F2.wireOp",EDGE,"E46");Q0=makeQuery(id+"F17.boolean.opBoolean","COPY",FACE,{"disambiguationData":[TD([makeQuery(id+"F3.opExtrude","SWEPT_FACE",FACE,{"disambiguationData":[OSD([sQuery(id+"F2.wireOp",EDGE,"E41")])]}),makeQuery(id+"F3.opExtrude","SWEPT_FACE",FACE,{"disambiguationData":[OSD([sQuery(id+"F2.wireOp",EDGE,"E42")])]}),makeQuery(id+"F3.opExtrude","SWEPT_FACE",FACE,{"disambiguationData":[OSD([sQuery(id+"F2.wireOp",EDGE,"E43")])]}),makeQuery(id+"F3.opExtrude","SWEPT_FACE",FACE,{"disambiguationData":[OSD([sQuery(id+"F2.wireOp",EDGE,"E44")])]}),makeQuery(id+"F3.opExtrude","SWEPT_FACE",FACE,{"disambiguationData":[OSD([subQ7]),TDD([makeQuery(id+"F2.imprint","IMPRINT",EDGE,{"disambiguationData":[TD([[makeQuery(id+"F2.imprint","INTERSECT",VERTEX,{"derivedFrom":[subQ7,subQ6]}),1.0]])],"derivedFrom":subQ7})])]}),makeQuery(id+"F3.opExtrude","SWEPT_FACE",FACE,{"disambiguationData":[OSD([subQ6])]}),makeQuery(id+"F3.opExtrude","SWEPT_FACE",FACE,{"disambiguationData":[OSD([sQuery(id+"F2.wireOp",EDGE,"E48")])]}),makeQuery(id+"F3.opExtrude","SWEPT_FACE",FACE,{"disambiguationData":[OSD([subQ5])]}),subQ4,makeQuery(id+"F17.opExtrude","SWEPT_FACE",FACE,{"disambiguationData":[OSD([subQ0])]}),makeQuery(id+"F17.opExtrude","SWEPT_FACE",FACE,{"disambiguationData":[OSD([subQ3])]}),makeQuery(id+"F17.opExtrude","SWEPT_FACE",FACE,{"disambiguationData":[OSD([subQ2])]}),makeQuery(id+"F17.opExtrude","SWEPT_FACE",FACE,{"disambiguationData":[OSD([subQ1])]})])],"derivedFrom":subQ4});}
            var sketch = newSketch(context, id + "F32", { "sketchPlane" : qUnion([Q0])});
            skLineSegment(sketch, "E111", {"start": v(-12165.6, 3970) * mm, "end": v(-12084.28, 3888.68) * mm});
            skLineSegment(sketch, "E112", {"start": v(-12084.28, 3888.68) * mm, "end": v(-11506.32, 4466.65) * mm});
            skLineSegment(sketch, "E113", {"start": v(-11506.32, 4466.65) * mm, "end": v(-11587.63, 4547.96) * mm});
            skLineSegment(sketch, "E114", {"start": v(-11587.63, 4547.96) * mm, "end": v(-12165.6, 3970) * mm});
            skLineSegment(sketch, "E115", {"start": v(-11411.81, 6791.22) * mm, "end": v(-11355.96, 6690.69) * mm});
            skLineSegment(sketch, "E116", {"start": v(-11355.96, 6690.69) * mm, "end": v(-10656.64, 7079.2) * mm});
            skLineSegment(sketch, "E117", {"start": v(-10656.64, 7079.2) * mm, "end": v(-10712.48, 7179.73) * mm});
            skLineSegment(sketch, "E118", {"start": v(-10712.48, 7179.73) * mm, "end": v(-11411.81, 6791.22) * mm});
            skLineSegment(sketch, "E119.bottom", {"start": v(-10475.85, 7105) * mm, "end": v(-9675.85, 7105) * mm});
            skLineSegment(sketch, "E119.top", {"start": v(-10475.85, 7220) * mm, "end": v(-9675.85, 7220) * mm});
            skLineSegment(sketch, "E119.left", {"start": v(-10475.85, 7105) * mm, "end": v(-10475.85, 7220) * mm});
            skLineSegment(sketch, "E119.right", {"start": v(-9675.85, 7105) * mm, "end": v(-9675.85, 7220) * mm});
            skLineSegment(sketch, "E120.1.0.0", {"start": v(-5475.85, 7105) * mm, "end": v(-5475.85, 7220) * mm});
            skLineSegment(sketch, "E120.1.0.1", {"start": v(-4675.85, 7105) * mm, "end": v(-4675.85, 7220) * mm});
            skLineSegment(sketch, "E120.1.0.2", {"start": v(-5475.85, 7220) * mm, "end": v(-4675.85, 7220) * mm});
            skLineSegment(sketch, "E120.1.0.3", {"start": v(-5475.85, 7105) * mm, "end": v(-4675.85, 7105) * mm});
            skLineSegment(sketch, "E120.direction1", {"start": v(-10475.85, 7105) * mm, "end": v(-5475.85, 7105) * mm, "construction": true});
            skLineSegment(sketch, "E121", {"start": v(-4184.96, 7056.43) * mm, "end": v(-4266.28, 6975.12) * mm});
            skLineSegment(sketch, "E122", {"start": v(-4266.28, 6975.12) * mm, "end": v(-3700.6, 6409.43) * mm});
            skLineSegment(sketch, "E123", {"start": v(-3700.6, 6409.43) * mm, "end": v(-3619.28, 6490.75) * mm});
            skLineSegment(sketch, "E124", {"start": v(-3619.28, 6490.75) * mm, "end": v(-4184.96, 7056.43) * mm});
            skLineSegment(sketch, "E125", {"start": v(-3223.94, 1806.67) * mm, "end": v(-3305.26, 1725.35) * mm});
            skLineSegment(sketch, "E126", {"start": v(-3305.26, 1725.35) * mm, "end": v(-2739.57, 1159.67) * mm});
            skLineSegment(sketch, "E127", {"start": v(-2739.57, 1159.67) * mm, "end": v(-2658.25, 1240.98) * mm});
            skLineSegment(sketch, "E128", {"start": v(-2658.25, 1240.98) * mm, "end": v(-3223.94, 1806.67) * mm});
            skSolve(sketch);
        }
        {
            var Q0;
            Q0 = qSketchRegion(id + "F32", true);
            var Q1;
            {var subQ4=sQuery(id+"F2.wireOp",EDGE,"E6");var subQ8=makeQuery(id+"F1.opExtrude","CAP_FACE",FACE,{"disambiguationData":[OSD([sQuery(id+"F0.wireOp",EDGE,"E0.bottom"),sQuery(id+"F0.wireOp",EDGE,"E0.top"),sQuery(id+"F0.wireOp",EDGE,"E0.left"),sQuery(id+"F0.wireOp",EDGE,"E0.right")])],"isStart":false});var subQ12=sQuery(id+"F2.wireOp",EDGE,"E1");Q1=makeQuery(id+"F15.boolean.opBoolean","MERGE",FACE,{"derivedFrom":[makeQuery(id+"F11.boolean.opBoolean","MERGE",FACE,{"derivedFrom":[makeQuery(id+"F3.boolean.opBoolean","SPLIT",FACE,{"disambiguationData":[TD([makeQuery(id+"F3.opExtrude","SWEPT_FACE",FACE,{"disambiguationData":[OSD([subQ12])]})])],"derivedFrom":subQ8}),makeQuery(id+"F3.boolean.opBoolean","SPLIT",FACE,{"disambiguationData":[TD([makeQuery(id+"F3.opExtrude","SWEPT_FACE",FACE,{"disambiguationData":[OSD([subQ4])]})])],"derivedFrom":subQ8})],"fromTools":[makeQuery(id+"F11.opExtrude","SWEPT_FACE",FACE,{"disambiguationData":[OSD([sQuery(id+"F10.wireOp",EDGE,"E59.bottom")])]})]})],"fromTools":[makeQuery(id+"F15.opExtrude","SWEPT_FACE",FACE,{"disambiguationData":[OSD([sQuery(id+"F14.wireOp",EDGE,"E66.bottom")])]})]});}
            extrude(context, id + "F33", {"entities" : qUnion([Q0]), "operationType" : NewBodyOperationType.REMOVE, "endBound" : BoundingType.UP_TO_SURFACE, "oppositeDirection" : true, "endBoundEntityFace" : qUnion([Q1]), "depth" : 25 * mm});
        }
        {
            var Q0;
            {var subQ4=sQuery(id+"F2.wireOp",EDGE,"E6");var subQ8=makeQuery(id+"F1.opExtrude","CAP_FACE",FACE,{"disambiguationData":[OSD([sQuery(id+"F0.wireOp",EDGE,"E0.bottom"),sQuery(id+"F0.wireOp",EDGE,"E0.top"),sQuery(id+"F0.wireOp",EDGE,"E0.left"),sQuery(id+"F0.wireOp",EDGE,"E0.right")])],"isStart":false});var subQ12=sQuery(id+"F2.wireOp",EDGE,"E1");var subQ13=sQuery(id+"F2.wireOp",EDGE,"E19");var subQ21=sQuery(id+"F2.wireOp",EDGE,"E41");var subQ25=sQuery(id+"F2.wireOp",EDGE,"E36");var subQ28=sQuery(id+"F2.wireOp",EDGE,"E32");var subQ31=sQuery(id+"F2.wireOp",EDGE,"E25");Q0=makeQuery(id+"F33.boolean.opBoolean","MERGE",FACE,{"derivedFrom":[makeQuery(id+"F3.boolean.opBoolean","SPLIT",FACE,{"disambiguationData":[TD([makeQuery(id+"F3.opExtrude","SWEPT_FACE",FACE,{"disambiguationData":[OSD([subQ31])]})])],"derivedFrom":subQ8}),makeQuery(id+"F3.boolean.opBoolean","SPLIT",FACE,{"disambiguationData":[TD([makeQuery(id+"F3.opExtrude","SWEPT_FACE",FACE,{"disambiguationData":[OSD([subQ28])]})])],"derivedFrom":subQ8}),makeQuery(id+"F3.boolean.opBoolean","SPLIT",FACE,{"disambiguationData":[TD([makeQuery(id+"F3.opExtrude","SWEPT_FACE",FACE,{"disambiguationData":[OSD([subQ25])]})])],"derivedFrom":subQ8}),makeQuery(id+"F3.boolean.opBoolean","SPLIT",FACE,{"disambiguationData":[TD([makeQuery(id+"F3.opExtrude","SWEPT_FACE",FACE,{"disambiguationData":[OSD([subQ21])]})])],"derivedFrom":subQ8}),makeQuery(id+"F3.boolean.opBoolean","SPLIT",FACE,{"disambiguationData":[TD([makeQuery(id+"F3.opExtrude","SWEPT_FACE",FACE,{"disambiguationData":[OSD([sQuery(id+"F2.wireOp",EDGE,"E16.0")])]})])],"derivedFrom":subQ8}),makeQuery(id+"F3.boolean.opBoolean","SPLIT",FACE,{"disambiguationData":[TD([makeQuery(id+"F3.opExtrude","SWEPT_FACE",FACE,{"disambiguationData":[OSD([subQ13])]})])],"derivedFrom":subQ8}),makeQuery(id+"F15.boolean.opBoolean","MERGE",FACE,{"derivedFrom":[makeQuery(id+"F11.boolean.opBoolean","MERGE",FACE,{"derivedFrom":[makeQuery(id+"F3.boolean.opBoolean","SPLIT",FACE,{"disambiguationData":[TD([makeQuery(id+"F3.opExtrude","SWEPT_FACE",FACE,{"disambiguationData":[OSD([subQ12])]})])],"derivedFrom":subQ8}),makeQuery(id+"F3.boolean.opBoolean","SPLIT",FACE,{"disambiguationData":[TD([makeQuery(id+"F3.opExtrude","SWEPT_FACE",FACE,{"disambiguationData":[OSD([subQ4])]})])],"derivedFrom":subQ8})],"fromTools":[makeQuery(id+"F11.opExtrude","SWEPT_FACE",FACE,{"disambiguationData":[OSD([sQuery(id+"F10.wireOp",EDGE,"E59.bottom")])]})]})],"fromTools":[makeQuery(id+"F15.opExtrude","SWEPT_FACE",FACE,{"disambiguationData":[OSD([sQuery(id+"F14.wireOp",EDGE,"E66.bottom")])]})]})],"fromTools":[makeQuery(id+"F33.opExtrude","CAP_FACE",FACE,{"disambiguationData":[OSD([sQuery(id+"F32.wireOp",EDGE,"E111"),sQuery(id+"F32.wireOp",EDGE,"E112"),sQuery(id+"F32.wireOp",EDGE,"E113"),sQuery(id+"F32.wireOp",EDGE,"E114")])],"isStart":false}),makeQuery(id+"F33.opExtrude","CAP_FACE",FACE,{"disambiguationData":[OSD([sQuery(id+"F32.wireOp",EDGE,"E115"),sQuery(id+"F32.wireOp",EDGE,"E116"),sQuery(id+"F32.wireOp",EDGE,"E117"),sQuery(id+"F32.wireOp",EDGE,"E118")])],"isStart":false}),makeQuery(id+"F33.opExtrude","CAP_FACE",FACE,{"disambiguationData":[OSD([sQuery(id+"F32.wireOp",EDGE,"E119.bottom"),sQuery(id+"F32.wireOp",EDGE,"E119.top"),sQuery(id+"F32.wireOp",EDGE,"E119.left"),sQuery(id+"F32.wireOp",EDGE,"E119.right")])],"isStart":false}),makeQuery(id+"F33.opExtrude","CAP_FACE",FACE,{"disambiguationData":[OSD([sQuery(id+"F32.wireOp",EDGE,"E120.1.0.0"),sQuery(id+"F32.wireOp",EDGE,"E120.1.0.1"),sQuery(id+"F32.wireOp",EDGE,"E120.1.0.2"),sQuery(id+"F32.wireOp",EDGE,"E120.1.0.3")])],"isStart":false}),makeQuery(id+"F33.opExtrude","CAP_FACE",FACE,{"disambiguationData":[OSD([sQuery(id+"F32.wireOp",EDGE,"E121"),sQuery(id+"F32.wireOp",EDGE,"E122"),sQuery(id+"F32.wireOp",EDGE,"E123"),sQuery(id+"F32.wireOp",EDGE,"E124")])],"isStart":false}),makeQuery(id+"F33.opExtrude","CAP_FACE",FACE,{"disambiguationData":[OSD([sQuery(id+"F32.wireOp",EDGE,"E125"),sQuery(id+"F32.wireOp",EDGE,"E126"),sQuery(id+"F32.wireOp",EDGE,"E127"),sQuery(id+"F32.wireOp",EDGE,"E128")])],"isStart":false})]});}
            var sketch = newSketch(context, id + "F34", { "sketchPlane" : qUnion([Q0])});
            skText(sketch, "E129", { "text": "WC", "fontName": "OpenSans-Regular.ttf"});
            skText(sketch, "E130", { "text": "Jean", "fontName": "OpenSans-Regular.ttf"});
            const initialGuessF34  = {"E129": [-14.5482, 2.32075, 1, 0, 0.68583], "E130": [-9.90355, 7.51316, 1, 0, 0.58333]};
            skSetInitialGuess(sketch, initialGuessF34);
            skSolve(sketch);
        }
        {
            var Q0;
            Q0 = qSketchRegion(id + "F34", true);
            extrude(context, id + "F35", {"entities" : qUnion([Q0]), "operationType" : NewBodyOperationType.ADD, "depth" : 25 * mm});
        }
        {
            var Q0;
            Q0=makeQuery(id+"F3.opExtrude","SWEPT_FACE",FACE,{"disambiguationData":[OSD([sQuery(id+"F2.wireOp",EDGE,"E12.left")])]});
            var sketch = newSketch(context, id + "F36", { "sketchPlane" : qUnion([Q0])});
            skText(sketch, "E131", { "text": "Bureaux BE", "fontName": "OpenSans-Regular.ttf"});
            const initialGuessF36  = {"E131": [2.068, 0.12192, 1, 0, 0.824]};
            skSetInitialGuess(sketch, initialGuessF36);
            skSolve(sketch);
        }
        {
            var Q0;
            Q0 = qSketchRegion(id + "F36", true);
            extrude(context, id + "F37", {"entities" : qUnion([Q0]), "operationType" : NewBodyOperationType.ADD, "depth" : 25 * mm});
        }
    });
